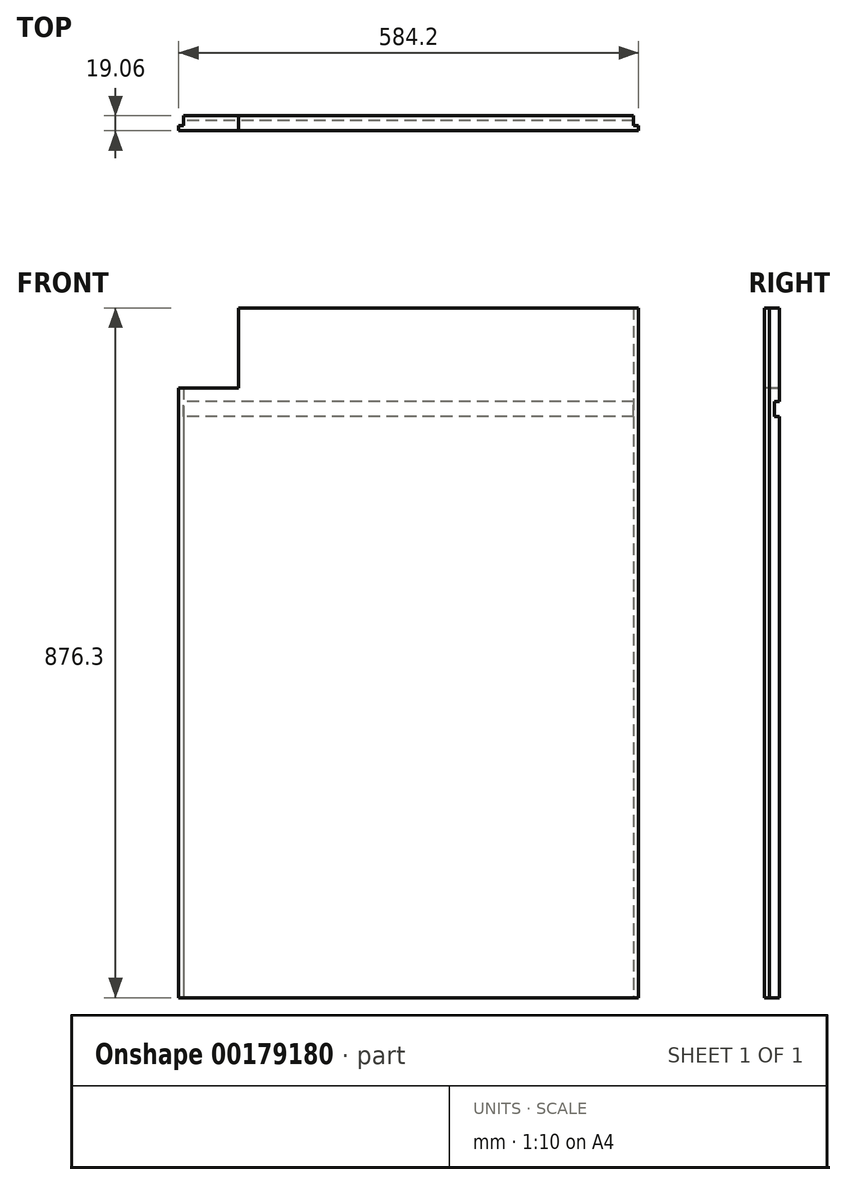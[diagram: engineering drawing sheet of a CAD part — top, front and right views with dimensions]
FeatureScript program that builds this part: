
annotation { "Feature Type Name" : "Feature", "Feature Type Description" : "" }
export const myFeature = defineFeature(function(context is Context, id is Id, definition is map)
    precondition{}
    {
        {
            var Q0;
            Q0=qCreatedBy(makeId("Front.planeOp"),FACE);
            var sketch = newSketch(context, id + "F0", { "sketchPlane" : qUnion([Q0])});
            skLineSegment(sketch, "E0.bottom", {"start": v(-247.9, 438.15) * mm, "end": v(336.3, 438.15) * mm});
            skLineSegment(sketch, "E0.top", {"start": v(-247.9, -438.15) * mm, "end": v(336.3, -438.15) * mm});
            skLineSegment(sketch, "E0.left", {"start": v(-247.9, 438.15) * mm, "end": v(-247.9, -438.15) * mm});
            skLineSegment(sketch, "E0.right", {"start": v(336.3, 438.15) * mm, "end": v(336.3, -438.15) * mm});
            skLineSegment(sketch, "E1", {"start": v(-247.9, 0) * mm, "end": v(336.3, 0) * mm});
            skSolve(sketch);
        }
        {
            var Q0;
            {var subQ0=sQuery(id+"F0.wireOp",EDGE,"E0.bottom");Q0=makeQuery(id+"F0.imprint","IMPRINT",FACE,{"disambiguationData":[TD([[makeQuery(id+"F0.imprint","IMPRINT",EDGE,{"derivedFrom":subQ0}),-1.0]])]});}
            var Q1;
            {var subQ0=sQuery(id+"F0.wireOp",EDGE,"E0.top");Q1=makeQuery(id+"F0.imprint","IMPRINT",FACE,{"disambiguationData":[TD([[makeQuery(id+"F0.imprint","IMPRINT",EDGE,{"derivedFrom":subQ0}),1.0]])]});}
            extrude(context, id + "F1", {"entities" : qUnion([Q0, Q1]), "depth" : 19.05 * mm, "symmetric" : true});
        }
        {
            var Q0;
            Q0=makeQuery(id+"F1.opExtrude","CAP_FACE",FACE,{"disambiguationData":[OSD([sQuery(id+"F0.wireOp",EDGE,"E0.bottom"),sQuery(id+"F0.wireOp",EDGE,"E0.top"),sQuery(id+"F0.wireOp",EDGE,"E0.left"),sQuery(id+"F0.wireOp",EDGE,"E0.right")])],"isStart":true});
            var sketch = newSketch(context, id + "F2", { "sketchPlane" : qUnion([Q0])});
            skLineSegment(sketch, "E2.bottom", {"start": v(-336.3, 438.15) * mm, "end": v(-329.95, 438.15) * mm});
            skLineSegment(sketch, "E2.top", {"start": v(-336.3, -438.15) * mm, "end": v(-329.95, -438.15) * mm});
            skLineSegment(sketch, "E2.left", {"start": v(-336.3, 438.15) * mm, "end": v(-336.3, -438.15) * mm});
            skLineSegment(sketch, "E2.right", {"start": v(-329.95, 438.15) * mm, "end": v(-329.95, -438.15) * mm});
            skLineSegment(sketch, "E3.bottom", {"start": v(247.9, 438.15) * mm, "end": v(241.55, 438.15) * mm});
            skLineSegment(sketch, "E3.top", {"start": v(247.9, -438.15) * mm, "end": v(241.55, -438.15) * mm});
            skLineSegment(sketch, "E3.left", {"start": v(247.9, 438.15) * mm, "end": v(247.9, -438.15) * mm});
            skLineSegment(sketch, "E3.right", {"start": v(241.55, 438.15) * mm, "end": v(241.55, -438.15) * mm});
            skSolve(sketch);
        }
        {
            var Q0;
            Q0 = qSketchRegion(id + "F2", true);
            extrude(context, id + "F3", {"entities" : qUnion([Q0]), "operationType" : NewBodyOperationType.REMOVE, "oppositeDirection" : true, "depth" : 12.7 * mm});
        }
        {
            var Q0;
            Q0=makeQuery(id+"F1.opExtrude","CAP_FACE",FACE,{"disambiguationData":[OSD([sQuery(id+"F0.wireOp",EDGE,"E0.bottom"),sQuery(id+"F0.wireOp",EDGE,"E0.top"),sQuery(id+"F0.wireOp",EDGE,"E0.left"),sQuery(id+"F0.wireOp",EDGE,"E0.right")])],"isStart":true});
            var sketch = newSketch(context, id + "F4", { "sketchPlane" : qUnion([Q0])});
            skLineSegment(sketch, "E4.bottom", {"start": v(-336.3, 300.04) * mm, "end": v(247.9, 300.04) * mm});
            skLineSegment(sketch, "E4.top", {"start": v(-336.3, 319.09) * mm, "end": v(247.9, 319.09) * mm});
            skLineSegment(sketch, "E4.left", {"start": v(-336.3, 300.04) * mm, "end": v(-336.3, 319.09) * mm});
            skLineSegment(sketch, "E4.right", {"start": v(247.9, 300.04) * mm, "end": v(247.9, 319.09) * mm});
            skSolve(sketch);
        }
        {
            var Q0;
            Q0 = qSketchRegion(id + "F4", true);
            extrude(context, id + "F5", {"entities" : qUnion([Q0]), "operationType" : NewBodyOperationType.REMOVE, "oppositeDirection" : true, "depth" : 6.35 * mm});
        }
        {
            var Q0;
            Q0=makeQuery(id+"F1.opExtrude","CAP_FACE",FACE,{"disambiguationData":[OSD([sQuery(id+"F0.wireOp",EDGE,"E0.bottom"),sQuery(id+"F0.wireOp",EDGE,"E0.top"),sQuery(id+"F0.wireOp",EDGE,"E0.left"),sQuery(id+"F0.wireOp",EDGE,"E0.right")])],"isStart":false});
            var sketch = newSketch(context, id + "F6", { "sketchPlane" : qUnion([Q0])});
            skLineSegment(sketch, "E5.bottom", {"start": v(-247.9, 438.15) * mm, "end": v(-171.7, 438.15) * mm});
            skLineSegment(sketch, "E5.top", {"start": v(-247.9, 336.55) * mm, "end": v(-171.7, 336.55) * mm});
            skLineSegment(sketch, "E5.left", {"start": v(-247.9, 438.15) * mm, "end": v(-247.9, 336.55) * mm});
            skLineSegment(sketch, "E5.right", {"start": v(-171.7, 438.15) * mm, "end": v(-171.7, 336.55) * mm});
            skSolve(sketch);
        }
        {
            var Q0;
            Q0=makeQuery(id+"F6.imprint","IMPRINT",FACE,{"disambiguationData":[TD([[makeQuery(id+"F6.imprint","IMPRINT",EDGE,{"derivedFrom":sQuery(id+"F6.wireOp",EDGE,"E5.bottom")}),-1.0]])]});
            extrude(context, id + "F7", {"entities" : qUnion([Q0]), "operationType" : NewBodyOperationType.REMOVE, "endBound" : BoundingType.THROUGH_ALL, "oppositeDirection" : true, "depth" : 25.4 * mm});
        }
    });
